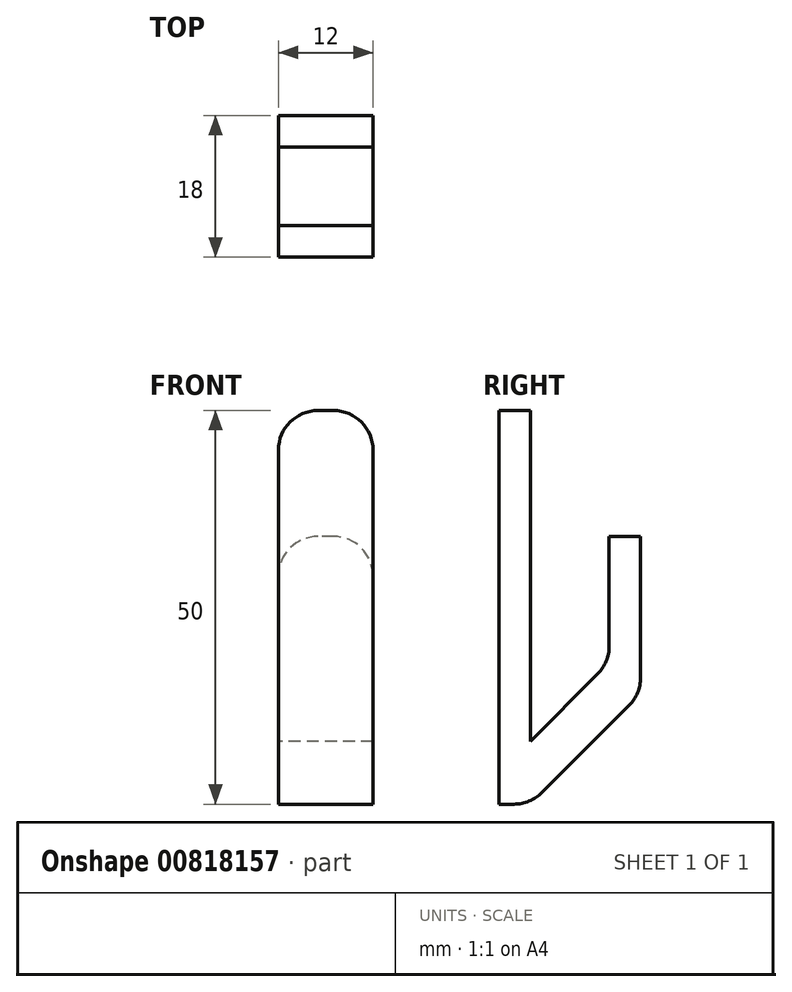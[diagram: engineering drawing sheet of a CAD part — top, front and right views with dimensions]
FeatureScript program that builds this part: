
annotation { "Feature Type Name" : "Feature", "Feature Type Description" : "" }
export const myFeature = defineFeature(function(context is Context, id is Id, definition is map)
    precondition{}
    {
        {
            var Q0;
            Q0=qCreatedBy(makeId("Front.planeOp"),FACE);
            var sketch = newSketch(context, id + "F0", { "sketchPlane" : qUnion([Q0])});
            skLineSegment(sketch, "E0", {"start": v(0, 0) * mm, "end": v(12, 0) * mm});
            skPoint(sketch, "E1", {"position": v(6, 0) * mm});
            skLineSegment(sketch, "E2", {"start": v(6, 0) * mm, "end": v(6, 50) * mm});
            skLineSegment(sketch, "E3", {"start": v(6, 50) * mm, "end": v(12, 50) * mm});
            skLineSegment(sketch, "E4", {"start": v(12, 50) * mm, "end": v(12, 0) * mm});
            skLineSegment(sketch, "E5", {"start": v(6, 50) * mm, "end": v(0, 50) * mm});
            skLineSegment(sketch, "E6", {"start": v(0, 50) * mm, "end": v(0, 0) * mm});
            skSolve(sketch);
        }
        {
            var Q0;
            {var subQ2=sQuery(id+"F0.wireOp",EDGE,"E2");Q0=makeQuery(id+"F0.imprint","IMPRINT",FACE,{"disambiguationData":[TD([[makeQuery(id+"F0.imprint","IMPRINT",EDGE,{"derivedFrom":subQ2}),-1.0]])]});}
            var Q1;
            {var subQ2=sQuery(id+"F0.wireOp",EDGE,"E2");Q1=makeQuery(id+"F0.imprint","IMPRINT",FACE,{"disambiguationData":[TD([[makeQuery(id+"F0.imprint","IMPRINT",EDGE,{"derivedFrom":subQ2}),1.0]])]});}
            extrude(context, id + "F1", {"entities" : qUnion([Q0, Q1]), "depth" : 4 * mm, "offsetDistance" : 25 * mm});
        }
        {
            var Q0;
            Q0=qCreatedBy(makeId("Right.planeOp"),FACE);
            var sketch = newSketch(context, id + "F2", { "sketchPlane" : qUnion([Q0])});
            skPoint(sketch, "E7", {"position": v(14, 14) * mm});
            skLineSegment(sketch, "E8", {"start": v(0, 0) * mm, "end": v(14, 14) * mm});
            skLineSegment(sketch, "E9", {"start": v(14, 14) * mm, "end": v(14, 34) * mm});
            skLineSegment(sketch, "E10", {"start": v(14, 34) * mm, "end": v(10, 34) * mm});
            skLineSegment(sketch, "E11", {"start": v(10, 34) * mm, "end": v(10, 18) * mm});
            skLineSegment(sketch, "E12", {"start": v(0, 0) * mm, "end": v(0, 8) * mm});
            skLineSegment(sketch, "E13", {"start": v(10, 18) * mm, "end": v(0, 8) * mm});
            skSolve(sketch);
        }
        {
            var Q0;
            Q0=makeQuery(id+"F2.imprint","IMPRINT",FACE,{"disambiguationData":[TD([[makeQuery(id+"F2.imprint","IMPRINT",EDGE,{"derivedFrom":sQuery(id+"F2.wireOp",EDGE,"E8")}),1.0]])]});
            extrude(context, id + "F3", {"entities" : qUnion([Q0]), "operationType" : NewBodyOperationType.ADD, "depth" : 12 * mm, "offsetDistance" : 25 * mm});
        }
        {
            var Q0;
            Q0=makeQuery(id+"F1.opExtrude","SWEPT_EDGE",EDGE,{"disambiguationData":[OSD([sQuery(id+"F0.wireOp",EDGE,"E5"),sQuery(id+"F0.wireOp",EDGE,"E6")])]});
            var Q1;
            Q1=makeQuery(id+"F1.opExtrude","SWEPT_EDGE",EDGE,{"disambiguationData":[OSD([sQuery(id+"F0.wireOp",EDGE,"E3"),sQuery(id+"F0.wireOp",EDGE,"E4")])]});
            var Q2;
            Q2=makeQuery(id+"F3.opExtrude","CAP_EDGE",EDGE,{"disambiguationData":[OSD([sQuery(id+"F2.wireOp",EDGE,"E10")])],"isStart":true});
            var Q3;
            Q3=makeQuery(id+"F3.opExtrude","CAP_EDGE",EDGE,{"disambiguationData":[OSD([sQuery(id+"F2.wireOp",EDGE,"E10")])],"isStart":false});
            var Q4;
            Q4=makeQuery(id+"F3.opExtrude","SWEPT_EDGE",EDGE,{"disambiguationData":[OSD([sQuery(id+"F2.wireOp",EDGE,"E11"),sQuery(id+"F2.wireOp",EDGE,"E13")])]});
            var Q5;
            Q5=makeQuery(id+"F3.opExtrude","SWEPT_EDGE",EDGE,{"disambiguationData":[OSD([sQuery(id+"F2.wireOp",EDGE,"E8"),sQuery(id+"F2.wireOp",EDGE,"E9")])]});
            var Q6;
            Q6=makeQuery(id+"F3.opExtrude","SWEPT_EDGE",EDGE,{"disambiguationData":[OSD([sQuery(id+"F2.wireOp",EDGE,"E12"),sQuery(id+"F2.wireOp",EDGE,"E13")])]});
            fillet(context, id + "F4", {"entities" : qUnion([Q0, Q1, Q2, Q3, Q4, Q5, Q6]), "radius" : 5 * mm, "tangentPropagation" : true, "allowEdgeOverflow" : false});
        }
        {
            var Q0;
            Q0=makeQuery(id+"F3.boolean.opBoolean","MERGE",EDGE,{"derivedFrom":[makeQuery(id+"F1.opExtrude","CAP_EDGE",EDGE,{"disambiguationData":[OSD([sQuery(id+"F0.wireOp",EDGE,"E0")])],"isStart":true}),makeQuery(id+"F3.opExtrude","SWEPT_EDGE",EDGE,{"disambiguationData":[OSD([sQuery(id+"F2.wireOp",EDGE,"E8"),sQuery(id+"F2.wireOp",EDGE,"E12")])]})]});
            fillet(context, id + "F5", {"entities" : qUnion([Q0]), "radius" : 5 * mm, "tangentPropagation" : true, "allowEdgeOverflow" : false});
        }
    });
